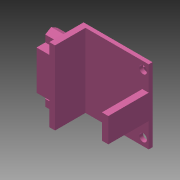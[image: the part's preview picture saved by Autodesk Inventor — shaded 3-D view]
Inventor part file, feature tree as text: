
AUTODESK INVENTOR PART (.ipt)
format: ipt  version: 2016 (Build 200138000, 138)  size: 156,160 bytes
history: native  units: mm
features: extrude x7, sketch x7
ambient origin geometry x8: Origin, YZ Plane, XZ Plane, XY Plane, X Axis, Y Axis, Z Axis, Center Point
bodies: Solid1 (feature_tree)
feature tree (14):
  extrude  "Extrusion1"  Depth=31.0mm
  extrude  "Extrusion2"  Depth=2.4mm
  extrude  "Extrusion3"  Depth=12.8mm
  extrude  "Extrusion4"  Depth=3.125mm
  extrude  "Extrusion5"  Depth=12.8mm TaperAngle=0.0deg
  extrude  "Extrusion6"  Depth=5.0mm
  extrude  "Extrusion7"  Depth=17.0mm
  sketch  "Sketch1"  dims[d0=29.0mm d1=31.0mm]
  sketch  "Sketch2"  dims[d2=1.6mm d3=0.0mm d4=2.4mm]
  sketch  "Sketch3"  dims[d5=12.8mm d6=0.0mm d7=2.375mm]
  sketch  "Sketch4"  dims[d8=3.125mm d9=3.125mm]
  sketch  "Sketch5"  dims[d10=3.25mm d11=12.8mm d12=0.0mm]
  sketch  "Sketch6"  dims[d13=7.65mm d14=5.0mm]
  sketch  "Sketch7"  dims[d15=3.78mm d16=3.78mm d17=6.0mm d18=0.0mm d19=3.8mm d20=8.0mm d21=16.5mm d22=8.0mm d23=0.0mm d24=5.0mm d25=5.0mm d26=3.0mm d27=0.0mm d28=10.3mm d29=2.7mm d30=0.0mm d31=17.0mm d32=0.0mm]
